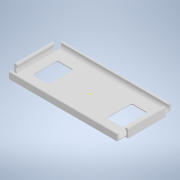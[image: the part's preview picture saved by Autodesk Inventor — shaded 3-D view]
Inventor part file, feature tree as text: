
AUTODESK INVENTOR PART (.ipt)
format: ipt  version: 2020 (Build 240168000, 168)  size: 285,184 bytes
history: native  units: mm
features: sketch x3, extrude x3, fillet x1, other x1
ambient origin geometry x8: Origin, YZ Plane, XZ Plane, XY Plane, X Axis, Y Axis, Z Axis, Center Point
bodies: Body1 (feature_tree)
feature tree (8):
  sketch  "Sketch2"  dims[d85=3600.0mm d86=0.0mm d87=1250.0mm d88=0.0mm]
  extrude  "Extrusion3"  Depth=1250.0mm TaperAngle=0.0deg
  extrude  "Extrusion4"  Depth=420.0mm
  extrude  "Extrusion5"  Depth=840.0mm
  fillet  "Fillet1"  Radius=1200.0mm
  sketch  "Sketch11"  dims[d92=550.0mm d93=380.0mm d94=1200.0mm d95=0.0mm d96=63.5mm d98=957.474029mm d99=957.474029mm d100=550.0mm d132=27.0mm d133=45.0mm d134=36.0mm d135=70.0mm d136=30.0mm d137=33.5mm d138=19.0mm d139=13.0mm d140=24.0mm d141=23.898419mm d145=23.136251mm d151=30.0mm d161=165.0mm d169=30.0mm d174=250.0mm d176=1843.326432mm d177=30.0mm d178=50.0mm d179=20.0mm d324=9.5mm d325=27.0mm d326=50.0mm d327=58.0mm d328=66.0mm d329=34.0mm d330=14.0mm d331=12.5mm d332=840.0mm d333=50.0mm d336=90.0deg d345=3686.652864mm d349=90.0deg d350=220.0mm d0=0.5mm d1=0.872665mm d2=0.5mm d3=0.872665mm d97=0.872665mm d109=0.5mm d110=0.872665mm d111=0.5mm d112=0.872665mm d113=0.872665mm d163=0.5mm d164=0.872665mm d165=0.5mm d166=0.872665mm]
  sketch  "Sketch4"  dims[d90=420.0mm d91=420.0mm]
  other  "Image2"
